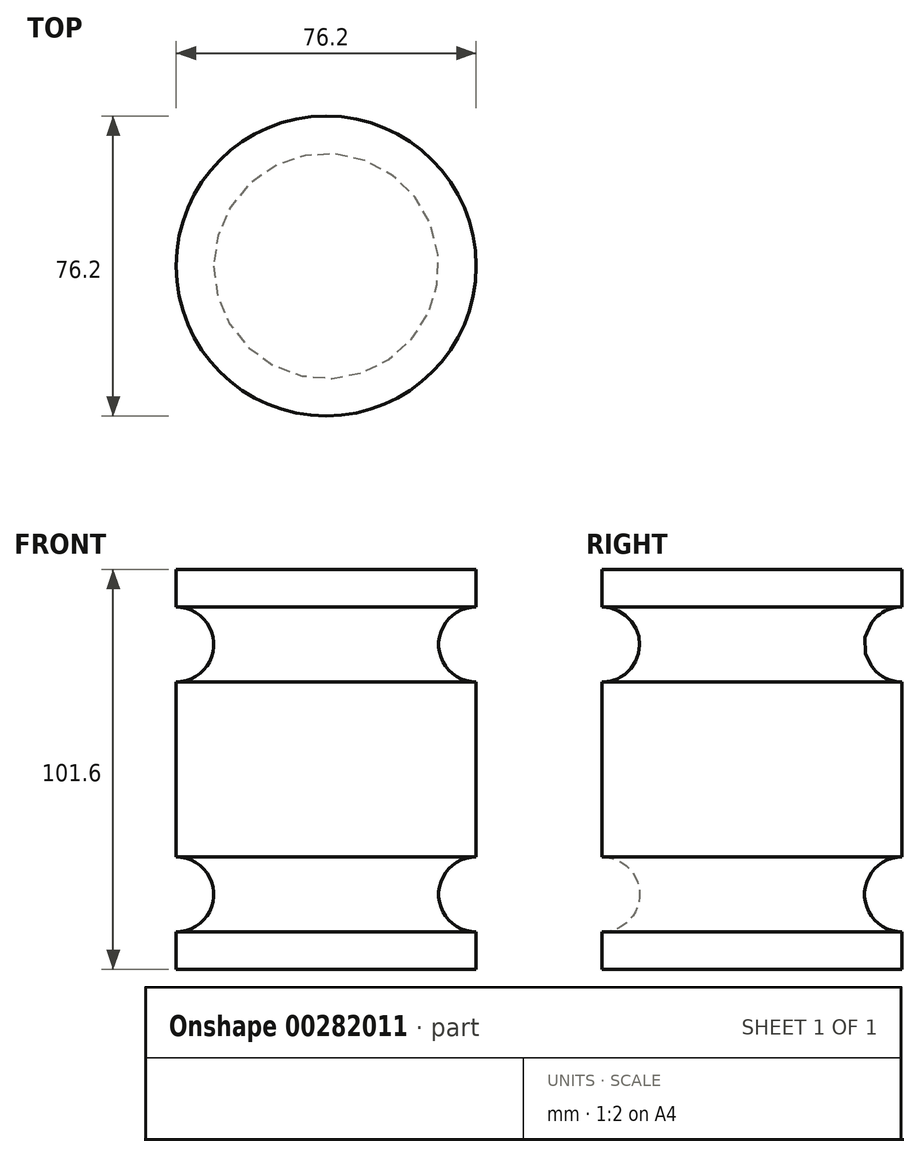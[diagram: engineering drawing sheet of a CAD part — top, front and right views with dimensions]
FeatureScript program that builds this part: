
annotation { "Feature Type Name" : "Feature", "Feature Type Description" : "" }
export const myFeature = defineFeature(function(context is Context, id is Id, definition is map)
    precondition{}
    {
        {
            var Q0;
            Q0=qCreatedBy(makeId("Front.planeOp"),FACE);
            var sketch = newSketch(context, id + "F0", { "sketchPlane" : qUnion([Q0])});
            skLineSegment(sketch, "E0.bottom", {"start": v(0, 0) * mm, "end": v(-38.1, 0) * mm});
            skLineSegment(sketch, "E0.top", {"start": v(0, 101.6) * mm, "end": v(-38.1, 101.6) * mm});
            skLineSegment(sketch, "E0.left", {"start": v(0, 0) * mm, "end": v(0, 9.53) * mm});
            skLineSegment(sketch, "E0.right", {"start": v(-38.1, 0) * mm, "end": v(-38.1, 101.6) * mm});
            skArc(sketch, "E1", {"start": v(0, 92.08) * mm, "mid": v(-9.53, 82.55) * mm, "end": v(0, 73.03) * mm});
            skArc(sketch, "E2", {"start": v(0, 28.58) * mm, "mid": v(-9.53, 19.05) * mm, "end": v(0, 9.53) * mm});
            skLineSegment(sketch, "E3.trimOffspring", {"start": v(0, 82.55) * mm, "end": v(0, 101.6) * mm});
            skLineSegment(sketch, "E4.trimOffspring", {"start": v(0, 19.05) * mm, "end": v(0, 73.03) * mm});
            skSolve(sketch);
        }
        {
            var Q0;
            Q0=makeQuery(id+"F0.imprint","IMPRINT",FACE,{"disambiguationData":[TD([[makeQuery(id+"F0.imprint","IMPRINT",EDGE,{"derivedFrom":sQuery(id+"F0.wireOp",EDGE,"E0.bottom")}),-1.0]])]});
            var Q1;
            Q1=sQuery(id+"F0.wireOp",EDGE,"E0.right");
            revolve(context, id + "F1", {"entities" : qUnion([Q0]), "axis" : qUnion([Q1]), "revolveType" : RevolveType.FULL});
        }
    });
